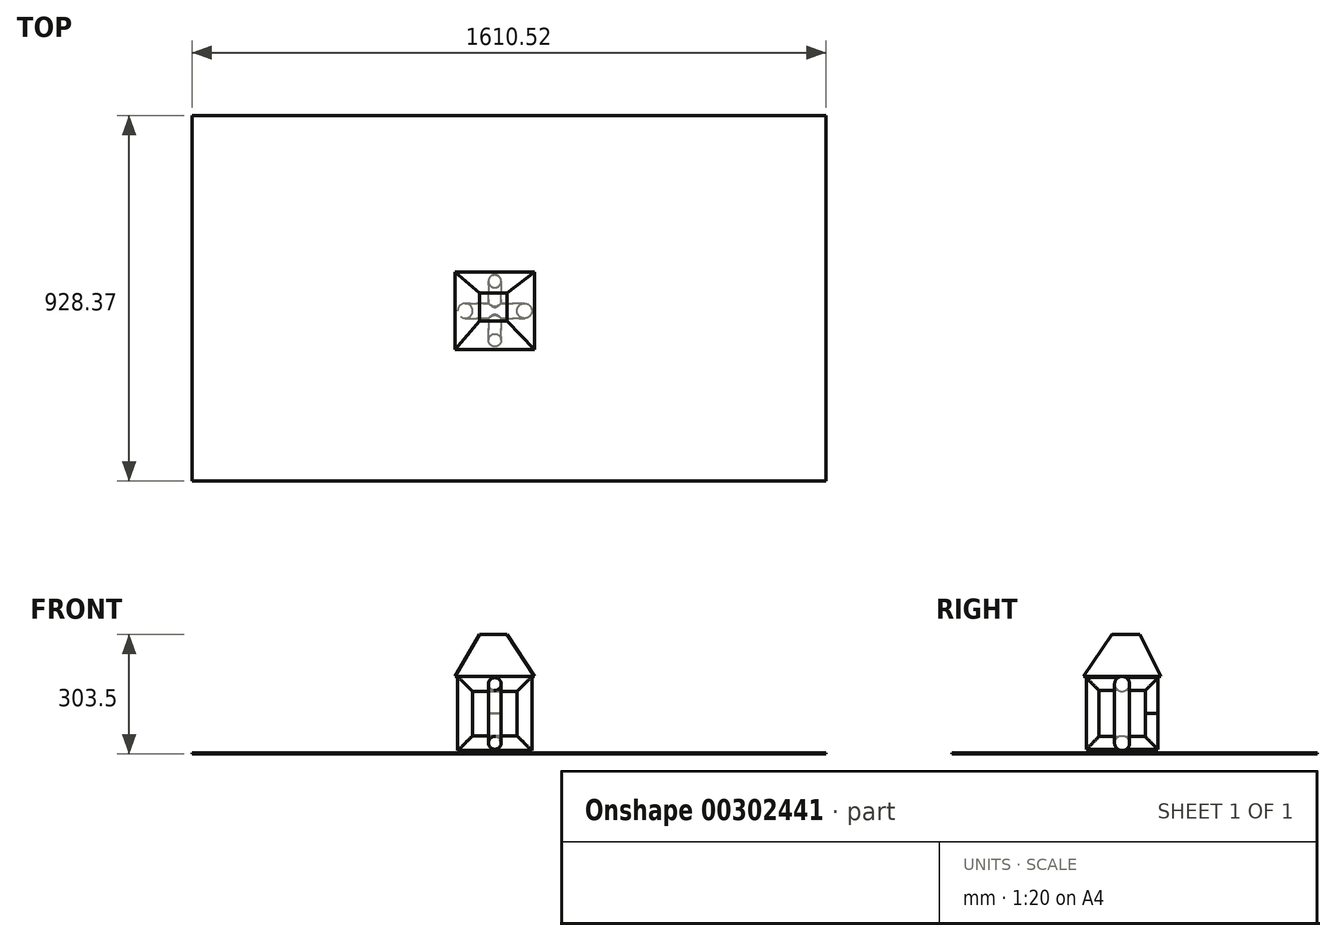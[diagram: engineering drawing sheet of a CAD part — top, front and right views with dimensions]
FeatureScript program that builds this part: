
annotation { "Feature Type Name" : "Feature", "Feature Type Description" : "" }
export const myFeature = defineFeature(function(context is Context, id is Id, definition is map)
    precondition{}
    {
        {
            var Q0;
            Q0=qCreatedBy(makeId("Top.planeOp"),FACE);
            var sketch = newSketch(context, id + "F0", { "sketchPlane" : qUnion([Q0])});
            skCircle(sketch, "E0", {"center": v(-75.3, 0) * mm, "radius": 19 * mm});
            skSolve(sketch);
        }
        {
            var Q0;
            Q0=qCreatedBy(makeId("Front.planeOp"),FACE);
            var sketch = newSketch(context, id + "F1", { "sketchPlane" : qUnion([Q0])});
            skLineSegment(sketch, "E1", {"start": v(-75.1, 0) * mm, "end": v(-75.1, 75.12) * mm});
            skLineSegment(sketch, "E2", {"start": v(-75.1, 75.12) * mm, "end": v(74.98, 75.12) * mm});
            skLineSegment(sketch, "E3", {"start": v(74.98, 75.12) * mm, "end": v(74.98, -74.95) * mm});
            skLineSegment(sketch, "E4", {"start": v(74.98, -74.95) * mm, "end": v(-75.1, -74.95) * mm});
            skLineSegment(sketch, "E5", {"start": v(-75.1, -74.95) * mm, "end": v(-75.1, 0) * mm});
            skSolve(sketch);
        }
        {
            var Q0;
            Q0=makeQuery(id+"F0.imprint","IMPRINT",FACE,{"disambiguationData":[TD([[makeQuery(id+"F0.imprint","IMPRINT",EDGE,{"derivedFrom":sQuery(id+"F0.wireOp",EDGE,"E0")}),1.0]])]});
            var Q1;
            Q1=sQuery(id+"F1.wireOp",EDGE,"E1");
            var Q2;
            Q2=sQuery(id+"F1.wireOp",EDGE,"E2");
            var Q3;
            Q3=sQuery(id+"F1.wireOp",EDGE,"E3");
            var Q4;
            Q4=sQuery(id+"F1.wireOp",EDGE,"E4");
            var Q5;
            Q5=sQuery(id+"F1.wireOp",EDGE,"E5");
            sweep(context, id + "F2", {"profiles" : qUnion([Q0]), "path" : qUnion([Q1, Q2, Q3, Q4, Q5])});
        }
        {
            var Q0;
            Q0=qCreatedBy(makeId("Top.planeOp"),FACE);
            var sketch = newSketch(context, id + "F3", { "sketchPlane" : qUnion([Q0])});
            skCircle(sketch, "E6", {"center": v(0, 75.3) * mm, "radius": 16.2 * mm});
            skSolve(sketch);
        }
        {
            var Q0;
            Q0=qCreatedBy(makeId("Right.planeOp"),FACE);
            var sketch = newSketch(context, id + "F4", { "sketchPlane" : qUnion([Q0])});
            skLineSegment(sketch, "E7", {"start": v(75.52, 0) * mm, "end": v(75.52, 75.38) * mm});
            skLineSegment(sketch, "E8", {"start": v(75.52, 75.38) * mm, "end": v(-74.85, 75.38) * mm});
            skLineSegment(sketch, "E9", {"start": v(-74.85, 75.38) * mm, "end": v(-74.85, -74.77) * mm});
            skLineSegment(sketch, "E10", {"start": v(-74.85, -74.77) * mm, "end": v(74.86, -74.77) * mm});
            skLineSegment(sketch, "E11", {"start": v(74.86, -74.77) * mm, "end": v(75.52, 0) * mm});
            skSolve(sketch);
        }
        {
            var Q0;
            Q0=makeQuery(id+"F3.imprint","IMPRINT",FACE,{"disambiguationData":[TD([[makeQuery(id+"F3.imprint","IMPRINT",EDGE,{"derivedFrom":sQuery(id+"F3.wireOp",EDGE,"E6")}),1.0]])]});
            var Q1;
            Q1=sQuery(id+"F4.wireOp",EDGE,"E8");
            var Q2;
            Q2=sQuery(id+"F4.wireOp",EDGE,"E7");
            var Q3;
            Q3=sQuery(id+"F4.wireOp",EDGE,"E9");
            var Q4;
            Q4=sQuery(id+"F4.wireOp",EDGE,"E10");
            var Q5;
            Q5=sQuery(id+"F4.wireOp",EDGE,"E11");
            sweep(context, id + "F5", {"operationType" : NewBodyOperationType.ADD, "profiles" : qUnion([Q0]), "path" : qUnion([Q1, Q2, Q3, Q4, Q5])});
        }
        {
            var Q0;
            Q0=qCreatedBy(makeId("Top.planeOp"),FACE);
            cPlane(context, id + "F6", {"entities" : qUnion([Q0]), "cplaneType" : CPlaneType.OFFSET, "offset" : 95 * mm, "width" : 150 * mm, "height" : 150 * mm});
        }
        {
            var Q0;
            Q0=qCreatedBy(id+"F6.planeOp",FACE);
            var sketch = newSketch(context, id + "F7", { "sketchPlane" : qUnion([Q0])});
            skLineSegment(sketch, "E12.bottom", {"start": v(-101.3, 98.5) * mm, "end": v(101.17, 98.5) * mm});
            skLineSegment(sketch, "E12.top", {"start": v(-101.3, -97.84) * mm, "end": v(101.17, -97.84) * mm});
            skLineSegment(sketch, "E12.left", {"start": v(-101.3, 98.5) * mm, "end": v(-101.3, -97.84) * mm});
            skLineSegment(sketch, "E12.right", {"start": v(101.17, 98.5) * mm, "end": v(101.17, -97.84) * mm});
            skSolve(sketch);
        }
        {
            var Q0;
            Q0=qCreatedBy(id+"F6.planeOp",FACE);
            cPlane(context, id + "F8", {"entities" : qUnion([Q0]), "cplaneType" : CPlaneType.OFFSET, "offset" : 106 * mm, "width" : 150 * mm, "height" : 150 * mm});
        }
        {
            var Q0;
            Q0=qCreatedBy(id+"F8.planeOp",FACE);
            var sketch = newSketch(context, id + "F9", { "sketchPlane" : qUnion([Q0])});
            skLineSegment(sketch, "E13.bottom", {"start": v(-38.27, 45.47) * mm, "end": v(30.8, 45.47) * mm});
            skLineSegment(sketch, "E13.top", {"start": v(-38.27, -25.49) * mm, "end": v(30.8, -25.49) * mm});
            skLineSegment(sketch, "E13.left", {"start": v(-38.27, 45.47) * mm, "end": v(-38.27, -25.49) * mm});
            skLineSegment(sketch, "E13.right", {"start": v(30.8, 45.47) * mm, "end": v(30.8, -25.49) * mm});
            skSolve(sketch);
        }
        {
            var Q0;
            Q0=makeQuery(id+"F9.imprint","IMPRINT",FACE,{"disambiguationData":[TD([[makeQuery(id+"F9.imprint","IMPRINT",EDGE,{"derivedFrom":sQuery(id+"F9.wireOp",EDGE,"E13.bottom")}),-1.0]])]});
            var Q1;
            Q1=makeQuery(id+"F7.imprint","IMPRINT",FACE,{"disambiguationData":[TD([[makeQuery(id+"F7.imprint","IMPRINT",EDGE,{"derivedFrom":sQuery(id+"F7.wireOp",EDGE,"E12.bottom")}),-1.0]])]});
            loft(context, id + "F10", {"sheetProfilesArray" : [{ "sheetProfileEntities" : qUnion([Q0]) }, { "sheetProfileEntities" : qUnion([Q1]) }]});
        }
        {
            var Q0;
            Q0=qCreatedBy(makeId("Top.planeOp"),FACE);
            cPlane(context, id + "F11", {"entities" : qUnion([Q0]), "cplaneType" : CPlaneType.OFFSET, "offset" : 100 * mm, "oppositeDirection" : true, "width" : 150 * mm, "height" : 150 * mm});
        }
        {
            var Q0;
            Q0=qCreatedBy(id+"F11.planeOp",FACE);
            var sketch = newSketch(context, id + "F12", { "sketchPlane" : qUnion([Q0])});
            skLineSegment(sketch, "E14.bottom", {"start": v(-769.15, -432.25) * mm, "end": v(841.37, -432.25) * mm});
            skLineSegment(sketch, "E14.top", {"start": v(-769.15, 496.12) * mm, "end": v(841.37, 496.12) * mm});
            skLineSegment(sketch, "E14.left", {"start": v(-769.15, -432.25) * mm, "end": v(-769.15, 496.12) * mm});
            skLineSegment(sketch, "E14.right", {"start": v(841.37, -432.25) * mm, "end": v(841.37, 496.12) * mm});
            skSolve(sketch);
        }
        {
            var Q0;
            Q0=makeQuery(id+"F12.imprint","IMPRINT",FACE,{"disambiguationData":[TD([[makeQuery(id+"F12.imprint","IMPRINT",EDGE,{"derivedFrom":sQuery(id+"F12.wireOp",EDGE,"E14.bottom")}),1.0]])]});
            extrude(context, id + "F13", {"entities" : qUnion([Q0]), "oppositeDirection" : true, "depth" : 2.5 * mm});
        }
    });
